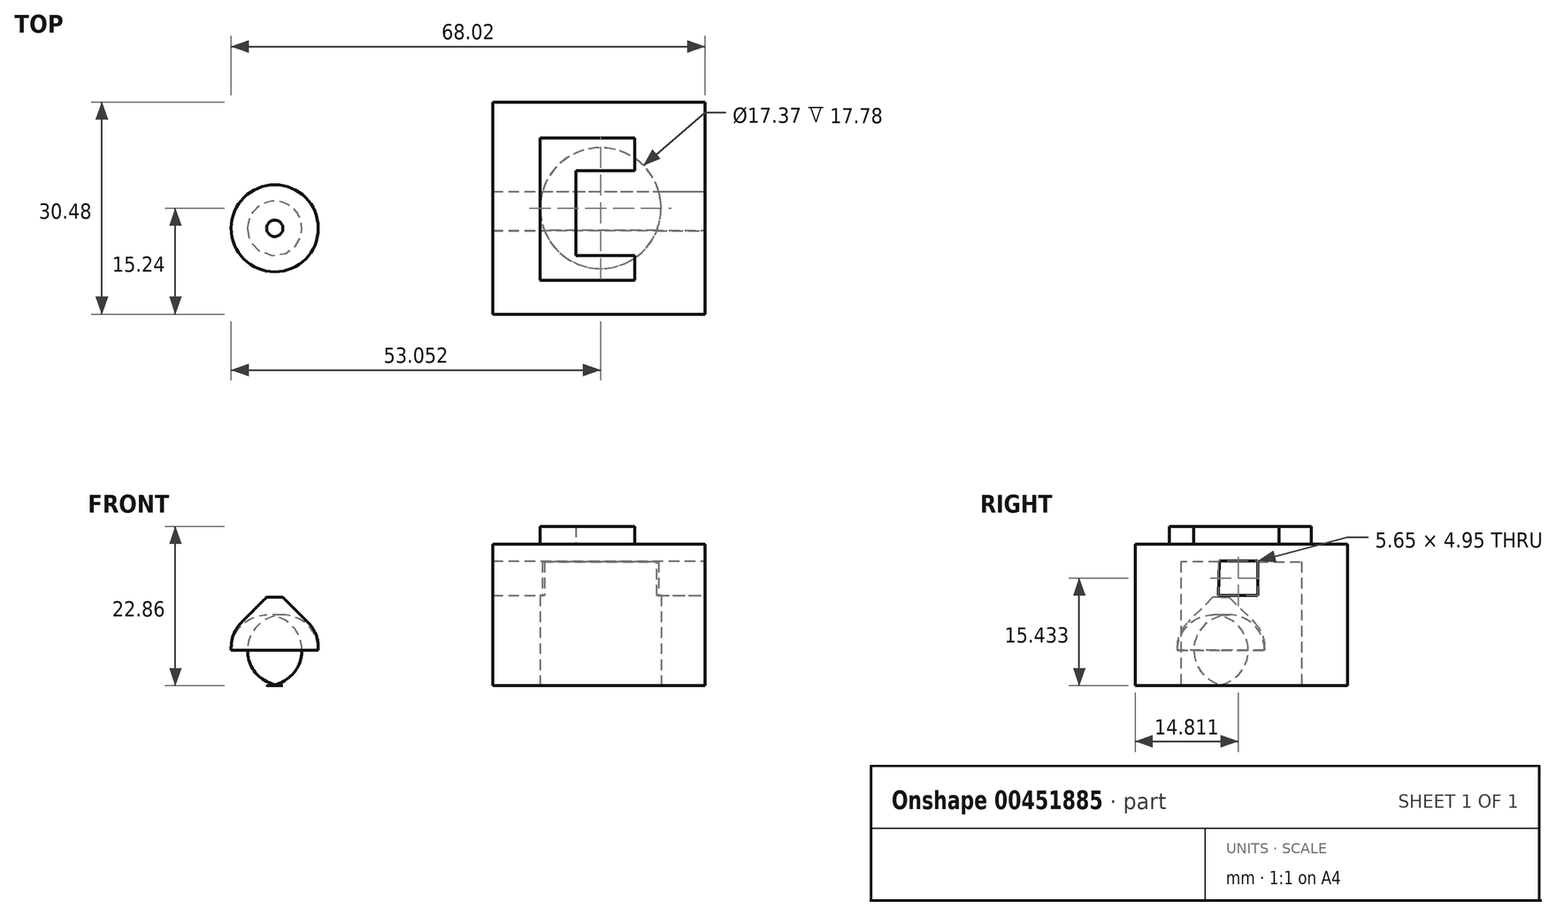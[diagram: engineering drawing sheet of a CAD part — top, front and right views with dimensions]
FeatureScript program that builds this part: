
annotation { "Feature Type Name" : "Feature", "Feature Type Description" : "" }
export const myFeature = defineFeature(function(context is Context, id is Id, definition is map)
    precondition{}
    {
        {
            var Q0;
            Q0=qCreatedBy(makeId("Top.planeOp"),FACE);
            var sketch = newSketch(context, id + "F0", { "sketchPlane" : qUnion([Q0])});
            skLineSegment(sketch, "E0", {"start": v(0, 0) * mm, "end": v(0, 30.48) * mm});
            skLineSegment(sketch, "E1", {"start": v(0, 30.48) * mm, "end": v(30.48, 30.48) * mm});
            skLineSegment(sketch, "E2", {"start": v(30.48, 30.48) * mm, "end": v(30.48, 0) * mm});
            skLineSegment(sketch, "E3", {"start": v(30.48, 0) * mm, "end": v(0, 0) * mm});
            skSolve(sketch);
        }
        {
            var Q0;
            Q0=makeQuery(id+"F0.imprint","IMPRINT",FACE,{"disambiguationData":[TD([[makeQuery(id+"F0.imprint","IMPRINT",EDGE,{"derivedFrom":sQuery(id+"F0.wireOp",EDGE,"E0")}),-1.0]])]});
            extrude(context, id + "F1", {"entities" : qUnion([Q0]), "depth" : 20.32 * mm});
        }
        {
            var Q0;
            Q0=makeQuery(id+"F1.opExtrude","CAP_FACE",FACE,{"disambiguationData":[OSD([sQuery(id+"F0.wireOp",EDGE,"E0"),sQuery(id+"F0.wireOp",EDGE,"E1"),sQuery(id+"F0.wireOp",EDGE,"E2"),sQuery(id+"F0.wireOp",EDGE,"E3")])],"isStart":true});
            var sketch = newSketch(context, id + "F2", { "sketchPlane" : qUnion([Q0])});
            skCircle(sketch, "E4", {"center": v(15.51, -15.24) * mm, "radius": 8.68 * mm});
            skPoint(sketch, "E4.centerSnap0", {"position": v(0, -15.24) * mm});
            skSolve(sketch);
        }
        {
            var Q0;
            Q0=makeQuery(id+"F2.imprint","IMPRINT",FACE,{"disambiguationData":[TD([[makeQuery(id+"F2.imprint","IMPRINT",EDGE,{"derivedFrom":sQuery(id+"F2.wireOp",EDGE,"E4")}),1.0]])]});
            extrude(context, id + "F3", {"entities" : qUnion([Q0]), "operationType" : NewBodyOperationType.REMOVE, "oppositeDirection" : true, "depth" : 17.78 * mm});
        }
        {
            var Q0;
            Q0=makeQuery(id+"F1.opExtrude","SWEPT_FACE",FACE,{"disambiguationData":[OSD([sQuery(id+"F0.wireOp",EDGE,"E2")])]});
            var sketch = newSketch(context, id + "F4", { "sketchPlane" : qUnion([Q0])});
            skLineSegment(sketch, "E5", {"start": v(11.99, 12.96) * mm, "end": v(17.64, 12.96) * mm});
            skLineSegment(sketch, "E6", {"start": v(17.64, 12.96) * mm, "end": v(17.64, 17.9) * mm});
            skLineSegment(sketch, "E7", {"start": v(17.64, 17.9) * mm, "end": v(12.08, 17.9) * mm});
            skLineSegment(sketch, "E8", {"start": v(12.08, 17.9) * mm, "end": v(11.99, 12.96) * mm});
            skSolve(sketch);
        }
        {
            var Q0;
            Q0 = qSketchRegion(id + "F4", true);
            extrude(context, id + "F5", {"entities" : qUnion([Q0]), "operationType" : NewBodyOperationType.REMOVE, "oppositeDirection" : true, "depth" : 35.56 * mm});
        }
        {
            var Q0;
            Q0=makeQuery(id+"F1.opExtrude","CAP_FACE",FACE,{"disambiguationData":[OSD([sQuery(id+"F0.wireOp",EDGE,"E0"),sQuery(id+"F0.wireOp",EDGE,"E1"),sQuery(id+"F0.wireOp",EDGE,"E2"),sQuery(id+"F0.wireOp",EDGE,"E3")])],"isStart":false});
            var sketch = newSketch(context, id + "F6", { "sketchPlane" : qUnion([Q0])});
            skLineSegment(sketch, "E9", {"start": v(20.41, 20.65) * mm, "end": v(11.97, 20.65) * mm});
            skLineSegment(sketch, "E10", {"start": v(11.97, 20.65) * mm, "end": v(11.97, 8.4) * mm});
            skLineSegment(sketch, "E11", {"start": v(11.97, 8.4) * mm, "end": v(20.41, 8.4) * mm});
            skLineSegment(sketch, "E12", {"start": v(20.41, 8.4) * mm, "end": v(20.41, 4.9) * mm});
            skLineSegment(sketch, "E13", {"start": v(20.41, 4.9) * mm, "end": v(6.8, 4.9) * mm});
            skLineSegment(sketch, "E14", {"start": v(6.8, 4.9) * mm, "end": v(6.8, 25.3) * mm});
            skLineSegment(sketch, "E15", {"start": v(6.8, 25.3) * mm, "end": v(20.41, 25.3) * mm});
            skLineSegment(sketch, "E16", {"start": v(20.41, 25.3) * mm, "end": v(20.41, 20.65) * mm});
            skSolve(sketch);
        }
        {
            var Q0;
            Q0=makeQuery(id+"F6.imprint","IMPRINT",FACE,{"disambiguationData":[TD([[makeQuery(id+"F6.imprint","IMPRINT",EDGE,{"derivedFrom":sQuery(id+"F6.wireOp",EDGE,"E9")}),-1.0]])]});
            extrude(context, id + "F7", {"entities" : qUnion([Q0]), "operationType" : NewBodyOperationType.ADD, "depth" : 2.54 * mm});
        }
        {
            var Q0;
            Q0=qCreatedBy(makeId("Top.planeOp"),FACE);
            var sketch = newSketch(context, id + "F8", { "sketchPlane" : qUnion([Q0])});
            skCircle(sketch, "E17", {"center": v(-31.28, 12.34) * mm, "radius": 6.25 * mm});
            skSolve(sketch);
        }
        {
            var Q0;
            Q0=makeQuery(id+"F8.imprint","IMPRINT",FACE,{"disambiguationData":[TD([[makeQuery(id+"F8.imprint","IMPRINT",EDGE,{"derivedFrom":sQuery(id+"F8.wireOp",EDGE,"E17")}),1.0]])]});
            extrude(context, id + "F9", {"entities" : qUnion([Q0]), "depth" : 12.7 * mm});
        }
        {
            var Q0;
            Q0=makeQuery(id+"F9.opExtrude","CAP_FACE",FACE,{"disambiguationData":[OSD([sQuery(id+"F8.wireOp",EDGE,"E17")])],"isStart":false});
            chamfer(context, id + "F10", {"entities" : qUnion([Q0]), "width" : 5.08 * mm, "tangentPropagation" : true});
        }
        {
            var Q0;
            Q0=makeQuery(id+"F9.opExtrude","SWEPT_FACE",FACE,{"disambiguationData":[OSD([sQuery(id+"F8.wireOp",EDGE,"E17")])]});
            fillet(context, id + "F11", {"entities" : qUnion([Q0]), "radius" : 5.08 * mm, "tangentPropagation" : true, "allowEdgeOverflow" : false});
        }
    });
